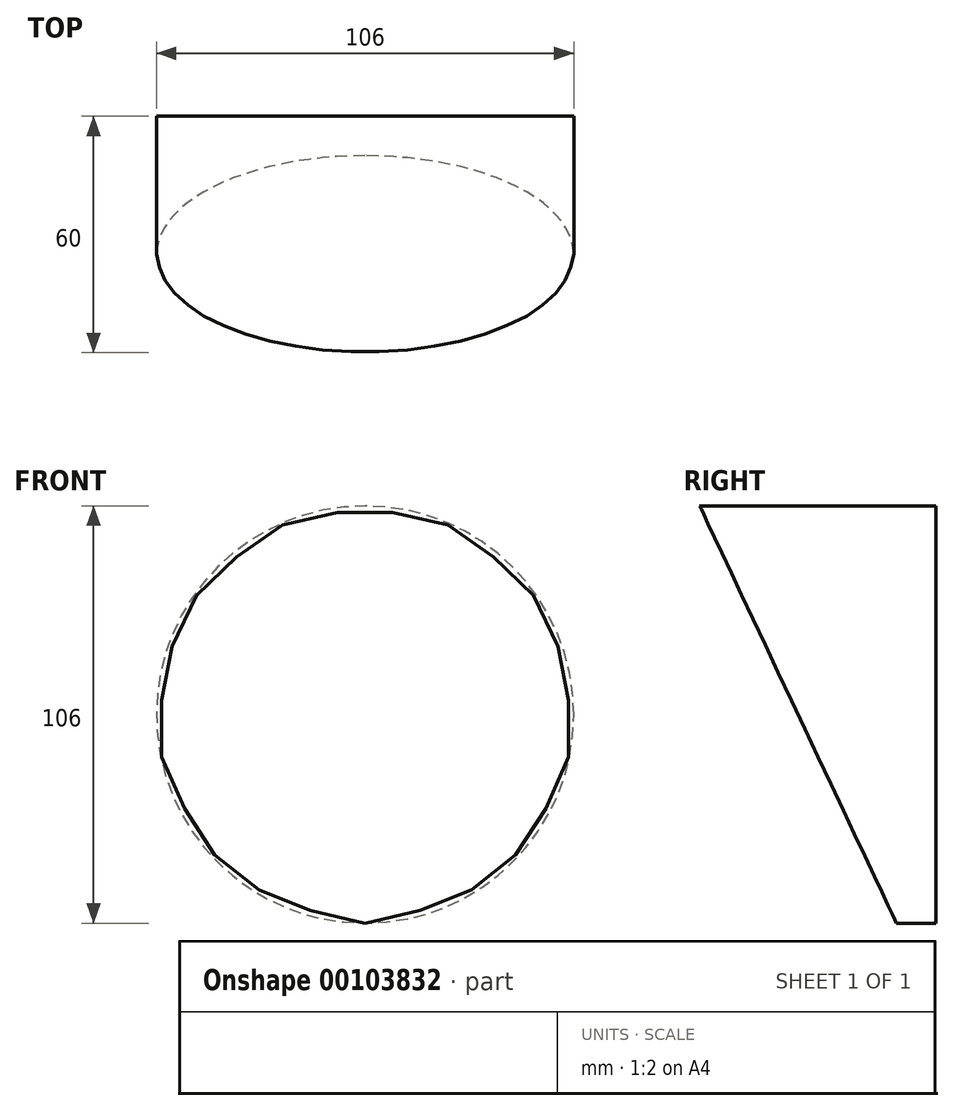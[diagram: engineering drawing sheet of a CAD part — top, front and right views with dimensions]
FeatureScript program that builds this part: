
annotation { "Feature Type Name" : "Feature", "Feature Type Description" : "" }
export const myFeature = defineFeature(function(context is Context, id is Id, definition is map)
    precondition{}
    {
        {
            var Q0;
            Q0=qCreatedBy(makeId("Front.planeOp"),FACE);
            var sketch = newSketch(context, id + "F0", { "sketchPlane" : qUnion([Q0])});
            skCircle(sketch, "E0", {"center": v(0, 0) * mm, "radius": 53 * mm});
            skSolve(sketch);
        }
        {
            var Q0;
            Q0=makeQuery(id+"F0.imprint","IMPRINT",FACE,{"disambiguationData":[TD([[makeQuery(id+"F0.imprint","IMPRINT",EDGE,{"derivedFrom":sQuery(id+"F0.wireOp",EDGE,"E0")}),1.0]])]});
            extrude(context, id + "F1", {"entities" : qUnion([Q0]), "depth" : 60 * mm});
        }
        {
            var Q0;
            Q0=qCreatedBy(makeId("Right.planeOp"),FACE);
            var sketch = newSketch(context, id + "F2", { "sketchPlane" : qUnion([Q0])});
            skLineSegment(sketch, "E1", {"start": v(0, 0) * mm, "end": v(0, -53) * mm, "construction": true});
            skLineSegment(sketch, "E2", {"start": v(0, 0) * mm, "end": v(0, 53) * mm, "construction": true});
            skLineSegment(sketch, "E3", {"start": v(0, 53) * mm, "end": v(-60, 53) * mm, "construction": true});
            skLineSegment(sketch, "E4", {"start": v(0, -53) * mm, "end": v(-10, -53) * mm, "construction": true});
            skLineSegment(sketch, "E5", {"start": v(-10, -53) * mm, "end": v(-60, 53) * mm, "construction": true});
            skLineSegment(sketch, "E6", {"start": v(-10, -53) * mm, "end": v(-60, -53) * mm});
            skLineSegment(sketch, "E7", {"start": v(-60, -53) * mm, "end": v(-60, 53) * mm});
            skLineSegment(sketch, "E8", {"start": v(-60, 53) * mm, "end": v(-10, -53) * mm});
            skSolve(sketch);
        }
        {
            var Q0;
            Q0 = qSketchRegion(id + "F2", true);
            extrude(context, id + "F3", {"entities" : qUnion([Q0]), "operationType" : NewBodyOperationType.REMOVE, "flatOperationType" : FlatOperationType.REMOVE, "endBound" : BoundingType.THROUGH_ALL, "offsetDistance" : 25 * mm, "depth" : 25 * mm, "hasSecondDirection" : true, "secondDirectionBound" : SecondDirectionBoundingType.THROUGH_ALL, "secondDirectionOppositeDirection" : true, "secondDirectionDepth" : 25 * mm, "domain" : OperationDomain.MODEL});
        }
    });
